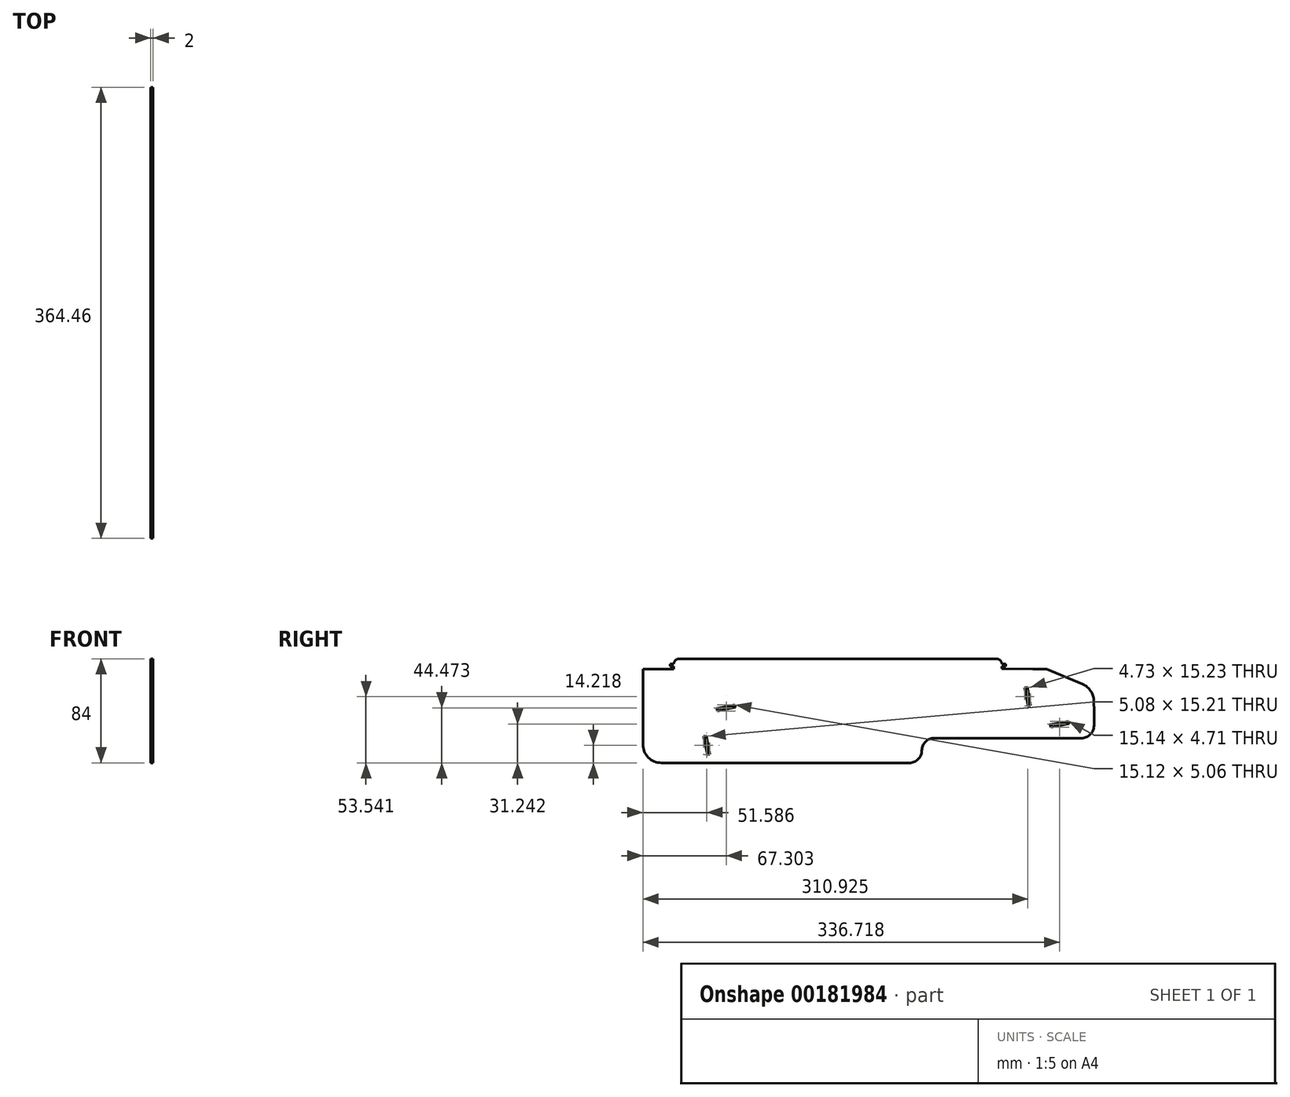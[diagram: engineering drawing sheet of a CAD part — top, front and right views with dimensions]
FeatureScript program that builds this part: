
annotation { "Feature Type Name" : "Feature", "Feature Type Description" : "" }
export const myFeature = defineFeature(function(context is Context, id is Id, definition is map)
    precondition{}
    {
        {
            var Q0;
            Q0=qCreatedBy(makeId("Right.planeOp"),FACE);
            var sketch = newSketch(context, id + "F0", { "sketchPlane" : qUnion([Q0])});
            skLineSegment(sketch, "E0.bottom", {"start": v(-177.1, 36.32) * mm, "end": v(90.9, 36.32) * mm});
            skLineSegment(sketch, "E0.top", {"start": v(-184.1, -43.68) * mm, "end": v(16.25, -43.68) * mm});
            skLineSegment(sketch, "E0.left", {"start": v(-199.1, 32.22) * mm, "end": v(-199.1, -28.68) * mm});
            skPoint(sketch, "E1.visualSharp", {"position": v(-199.1, -43.68) * mm});
            skArc(sketch, "E1.filletArc", {"start": v(-199.1, -28.68) * mm, "mid": v(-194.71, -39.28) * mm, "end": v(-184.1, -43.68) * mm});
            skLineSegment(sketch, "E2", {"start": v(-109.97, 6.32) * mm, "end": v(-154.06, -2.68) * mm});
            skLineSegment(sketch, "E3", {"start": v(-154.06, -2.68) * mm, "end": v(-147.04, -37.07) * mm});
            skLineSegment(sketch, "E4", {"start": v(-124.67, 3.32) * mm, "end": v(-124.25, 1.26) * mm});
            skLineSegment(sketch, "E5", {"start": v(-124.25, 1.26) * mm, "end": v(-138.95, -1.74) * mm});
            skLineSegment(sketch, "E6", {"start": v(-138.95, -1.74) * mm, "end": v(-139.37, 0.32) * mm});
            skLineSegment(sketch, "E7", {"start": v(159.94, -9.5) * mm, "end": v(125.49, -15.68) * mm});
            skLineSegment(sketch, "E8", {"start": v(125.49, -15.68) * mm, "end": v(115.65, -17.44) * mm});
            skPoint(sketch, "E9", {"position": v(137.8, -13.47) * mm});
            skLineSegment(sketch, "E10", {"start": v(145.18, -12.15) * mm, "end": v(144.8, -10.08) * mm});
            skLineSegment(sketch, "E11", {"start": v(144.8, -10.08) * mm, "end": v(130.04, -12.73) * mm});
            skLineSegment(sketch, "E12", {"start": v(130.04, -12.73) * mm, "end": v(130.41, -14.8) * mm});
            skLineSegment(sketch, "E13", {"start": v(115.65, -17.44) * mm, "end": v(109.45, 17.1) * mm});
            skLineSegment(sketch, "E14", {"start": v(165.35, -13.68) * mm, "end": v(165.35, -1.84) * mm});
            skLineSegment(sketch, "E15", {"start": v(127.1, 32.12) * mm, "end": v(156.11, 19.93) * mm});
            skLineSegment(sketch, "E16", {"start": v(165.3, 6.2) * mm, "end": v(165.35, -1.84) * mm});
            skPoint(sketch, "E17.visualSharp", {"position": v(165.23, 16.1) * mm});
            skArc(sketch, "E17.filletArc", {"start": v(165.3, 6.2) * mm, "mid": v(162.76, 14.44) * mm, "end": v(156.11, 19.93) * mm});
            skLineSegment(sketch, "E18", {"start": v(90.9, 36.32) * mm, "end": v(90.9, 36.32) * mm});
            skLineSegment(sketch, "E19", {"start": v(86.9, 40.32) * mm, "end": v(-170.1, 40.32) * mm});
            skLineSegment(sketch, "E20", {"start": v(-174.1, 36.32) * mm, "end": v(-174.1, 36.32) * mm});
            skPoint(sketch, "E21.visualSharp", {"position": v(-174.1, 40.32) * mm});
            skArc(sketch, "E21.filletArc", {"start": v(-170.1, 40.32) * mm, "mid": v(-172.93, 39.15) * mm, "end": v(-174.1, 36.32) * mm});
            skPoint(sketch, "E22.visualSharp", {"position": v(90.9, 40.32) * mm});
            skArc(sketch, "E22.filletArc", {"start": v(90.9, 36.32) * mm, "mid": v(89.72, 39.15) * mm, "end": v(86.9, 40.32) * mm});
            skLineSegment(sketch, "E23", {"start": v(109.45, 17.1) * mm, "end": v(111.52, 17.48) * mm});
            skLineSegment(sketch, "E24", {"start": v(111.52, 17.48) * mm, "end": v(114.18, 2.64) * mm});
            skLineSegment(sketch, "E25", {"start": v(114.18, 2.64) * mm, "end": v(112.12, 2.24) * mm});
            skLineSegment(sketch, "E26", {"start": v(90.9, 32.32) * mm, "end": v(90.9, 36.32) * mm});
            skLineSegment(sketch, "E27", {"start": v(-174.1, 36.32) * mm, "end": v(-174.1, 32.22) * mm});
            skLineSegment(sketch, "E28", {"start": v(-174.1, 34.27) * mm, "end": v(-177.1, 34.27) * mm});
            skLineSegment(sketch, "E29", {"start": v(-177.1, 34.27) * mm, "end": v(-177.1, 36.32) * mm});
            skLineSegment(sketch, "E30", {"start": v(137.8, -13.47) * mm, "end": v(124.83, 58.8) * mm});
            skLineSegment(sketch, "E31", {"start": v(-132.02, 1.82) * mm, "end": v(-124.08, -37.08) * mm});
            skLineSegment(sketch, "E32", {"start": v(-124.08, -37.08) * mm, "end": v(132.63, 15.32) * mm});
            skLineSegment(sketch, "E33", {"start": v(-147.04, -37.07) * mm, "end": v(-144.98, -36.65) * mm});
            skLineSegment(sketch, "E34", {"start": v(-150.06, -22.27) * mm, "end": v(-148, -21.85) * mm});
            skLineSegment(sketch, "E35", {"start": v(-144.98, -36.65) * mm, "end": v(-148, -21.85) * mm});
            skLineSegment(sketch, "E36", {"start": v(115.9, 32.12) * mm, "end": v(90.9, 32.32) * mm});
            skLineSegment(sketch, "E37", {"start": v(-174.1, 32.22) * mm, "end": v(-199.1, 32.22) * mm});
            skLineSegment(sketch, "E38", {"start": v(115.9, 32.12) * mm, "end": v(127.1, 32.12) * mm});
            skLineSegment(sketch, "E39", {"start": v(155.35, -23.68) * mm, "end": v(36.25, -23.68) * mm});
            skLineSegment(sketch, "E40", {"start": v(26.25, -33.68) * mm, "end": v(26.25, -33.68) * mm});
            skArc(sketch, "E41.filletArc", {"start": v(36.25, -23.68) * mm, "mid": v(29.18, -26.6) * mm, "end": v(26.25, -33.68) * mm});
            skArc(sketch, "E42.filletArc", {"start": v(16.25, -43.68) * mm, "mid": v(23.32, -40.75) * mm, "end": v(26.25, -33.68) * mm});
            skArc(sketch, "E43.filletArc", {"start": v(155.35, -23.68) * mm, "mid": v(162.42, -20.75) * mm, "end": v(165.35, -13.68) * mm});
            skPoint(sketch, "E44", {"position": v(103.4, 32.22) * mm});
            skPoint(sketch, "E45", {"position": v(-186.6, 32.22) * mm});
            skPoint(sketch, "E46", {"position": v(90.9, 34.32) * mm});
            skLineSegment(sketch, "E47.bottom", {"start": v(90.9, 34.32) * mm, "end": v(93.9, 34.32) * mm});
            skLineSegment(sketch, "E47.top", {"start": v(90.9, 36.32) * mm, "end": v(93.9, 36.32) * mm});
            skLineSegment(sketch, "E47.left", {"start": v(90.9, 34.32) * mm, "end": v(90.9, 36.32) * mm});
            skLineSegment(sketch, "E47.right", {"start": v(93.9, 34.32) * mm, "end": v(93.9, 36.32) * mm});
            skSolve(sketch);
        }
        {
            var Q0;
            Q0=makeQuery(id+"F0.imprint","IMPRINT",FACE,{"disambiguationData":[TD([[makeQuery(id+"F0.imprint","IMPRINT",EDGE,{"derivedFrom":sQuery(id+"F0.wireOp",EDGE,"E0.top")}),1.0]])]});
            var Q1;
            {var subQ4=sQuery(id+"F0.wireOp",EDGE,"E8");Q1=makeQuery(id+"F0.imprint","IMPRINT",FACE,{"disambiguationData":[TD([[makeQuery(id+"F0.imprint","IMPRINT",EDGE,{"derivedFrom":subQ4}),-1.0]])]});}
            var Q2;
            Q2=makeQuery(id+"F0.imprint","IMPRINT",FACE,{"disambiguationData":[TD([[makeQuery(id+"F0.imprint","IMPRINT",EDGE,{"derivedFrom":sQuery(id+"F0.wireOp",EDGE,"E19")}),1.0]])]});
            var Q3;
            Q3=makeQuery(id+"F0.imprint","IMPRINT",FACE,{"disambiguationData":[TD([[makeQuery(id+"F0.imprint","IMPRINT",EDGE,{"derivedFrom":sQuery(id+"F0.wireOp",EDGE,"E47.bottom")}),1.0]])]});
            var Q4;
            {var subQ4=sQuery(id+"F0.wireOp",EDGE,"E28");Q4=makeQuery(id+"F0.imprint","IMPRINT",FACE,{"disambiguationData":[TD([[makeQuery(id+"F0.imprint","IMPRINT",EDGE,{"derivedFrom":subQ4}),-1.0]])]});}
            extrude(context, id + "F1", {"entities" : qUnion([Q0, Q1, Q2, Q3, Q4]), "depth" : 2 * mm});
        }
    });
